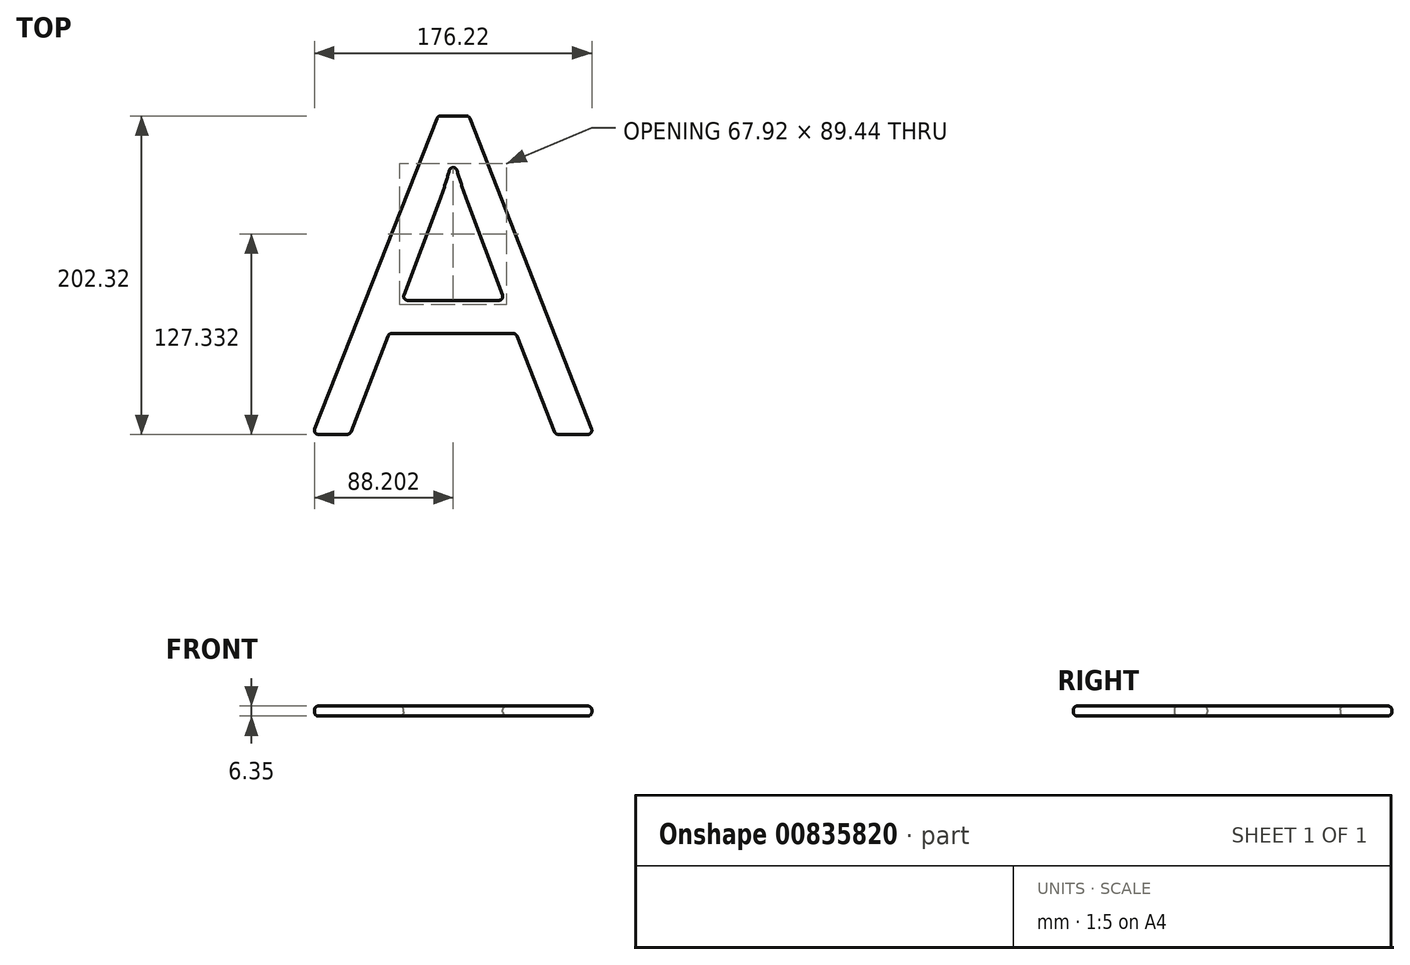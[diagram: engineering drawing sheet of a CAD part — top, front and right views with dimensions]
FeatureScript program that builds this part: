
annotation { "Feature Type Name" : "Feature", "Feature Type Description" : "" }
export const myFeature = defineFeature(function(context is Context, id is Id, definition is map)
    precondition{}
    {
        {
            var Q0;
            Q0=qCreatedBy(makeId("Top.planeOp"),FACE);
            var sketch = newSketch(context, id + "F0", { "sketchPlane" : qUnion([Q0])});
            skText(sketch, "E0", { "text": "A", "fontName": "OpenSans-Regular.ttf"});
            const initialGuessF0  = {"E0": [0, 0, 1, 0, 0.2032]};
            skSetInitialGuess(sketch, initialGuessF0);
            skSolve(sketch);
        }
        {
            var Q0;
            Q0=makeQuery(id+"F0.imprint","IMPRINT",FACE,{"disambiguationData":[TD([[makeQuery(id+"F0.imprint","IMPRINT",EDGE,{"derivedFrom":sQuery(id+"F0.wireOp",EDGE,"E0.sketch_text.stroke-0")}),-1.0]])]});
            extrude(context, id + "F1", {"entities" : qUnion([Q0]), "depth" : 6.35 * mm, "offsetDistance" : 25.4 * mm});
        }
        {
            var Q0;
            Q0=makeQuery(id+"F1.opExtrude","SWEPT_FACE",FACE,{"disambiguationData":[OSD([sQuery(id+"F0.wireOp",EDGE,"E0.sketch_text.stroke-6")])]});
            var Q1;
            Q1=makeQuery(id+"F1.opExtrude","SWEPT_FACE",FACE,{"disambiguationData":[OSD([sQuery(id+"F0.wireOp",EDGE,"E0.sketch_text.stroke-5")])]});
            var Q2;
            Q2=makeQuery(id+"F1.opExtrude","SWEPT_FACE",FACE,{"disambiguationData":[OSD([sQuery(id+"F0.wireOp",EDGE,"E0.sketch_text.stroke-4")])]});
            var Q3;
            Q3=makeQuery(id+"F1.opExtrude","SWEPT_FACE",FACE,{"disambiguationData":[OSD([sQuery(id+"F0.wireOp",EDGE,"E0.sketch_text.stroke-8")])]});
            var Q4;
            Q4=makeQuery(id+"F1.opExtrude","SWEPT_FACE",FACE,{"disambiguationData":[OSD([sQuery(id+"F0.wireOp",EDGE,"E0.sketch_text.stroke-9")])]});
            var Q5;
            Q5=makeQuery(id+"F1.opExtrude","SWEPT_FACE",FACE,{"disambiguationData":[OSD([sQuery(id+"F0.wireOp",EDGE,"E0.sketch_text.stroke-10")])]});
            var Q6;
            Q6=makeQuery(id+"F1.opExtrude","SWEPT_FACE",FACE,{"disambiguationData":[OSD([sQuery(id+"F0.wireOp",EDGE,"E0.sketch_text.stroke-11")])]});
            var Q7;
            Q7=makeQuery(id+"F1.opExtrude","SWEPT_FACE",FACE,{"disambiguationData":[OSD([sQuery(id+"F0.wireOp",EDGE,"E0.sketch_text.stroke-1")])]});
            var Q8;
            Q8=makeQuery(id+"F1.opExtrude","SWEPT_FACE",FACE,{"disambiguationData":[OSD([sQuery(id+"F0.wireOp",EDGE,"E0.sketch_text.stroke-12")])]});
            var Q9;
            Q9=makeQuery(id+"F1.opExtrude","SWEPT_FACE",FACE,{"disambiguationData":[OSD([sQuery(id+"F0.wireOp",EDGE,"E0.sketch_text.stroke-2")])]});
            var Q10;
            Q10=makeQuery(id+"F1.opExtrude","SWEPT_FACE",FACE,{"disambiguationData":[OSD([sQuery(id+"F0.wireOp",EDGE,"E0.sketch_text.stroke-3")])]});
            var Q11;
            Q11=makeQuery(id+"F1.opExtrude","SWEPT_FACE",FACE,{"disambiguationData":[OSD([sQuery(id+"F0.wireOp",EDGE,"E0.sketch_text.stroke-7")])]});
            var Q12;
            Q12=makeQuery(id+"F1.opExtrude","SWEPT_FACE",FACE,{"disambiguationData":[OSD([sQuery(id+"F0.wireOp",EDGE,"E0.sketch_text.stroke-0")])]});
            fillet(context, id + "F2", {"entities" : qUnion([Q0, Q1, Q2, Q3, Q4, Q5, Q6, Q7, Q8, Q9, Q10, Q11, Q12]), "radius" : 2.54 * mm, "tangentPropagation" : true, "allowEdgeOverflow" : false});
        }
    });
